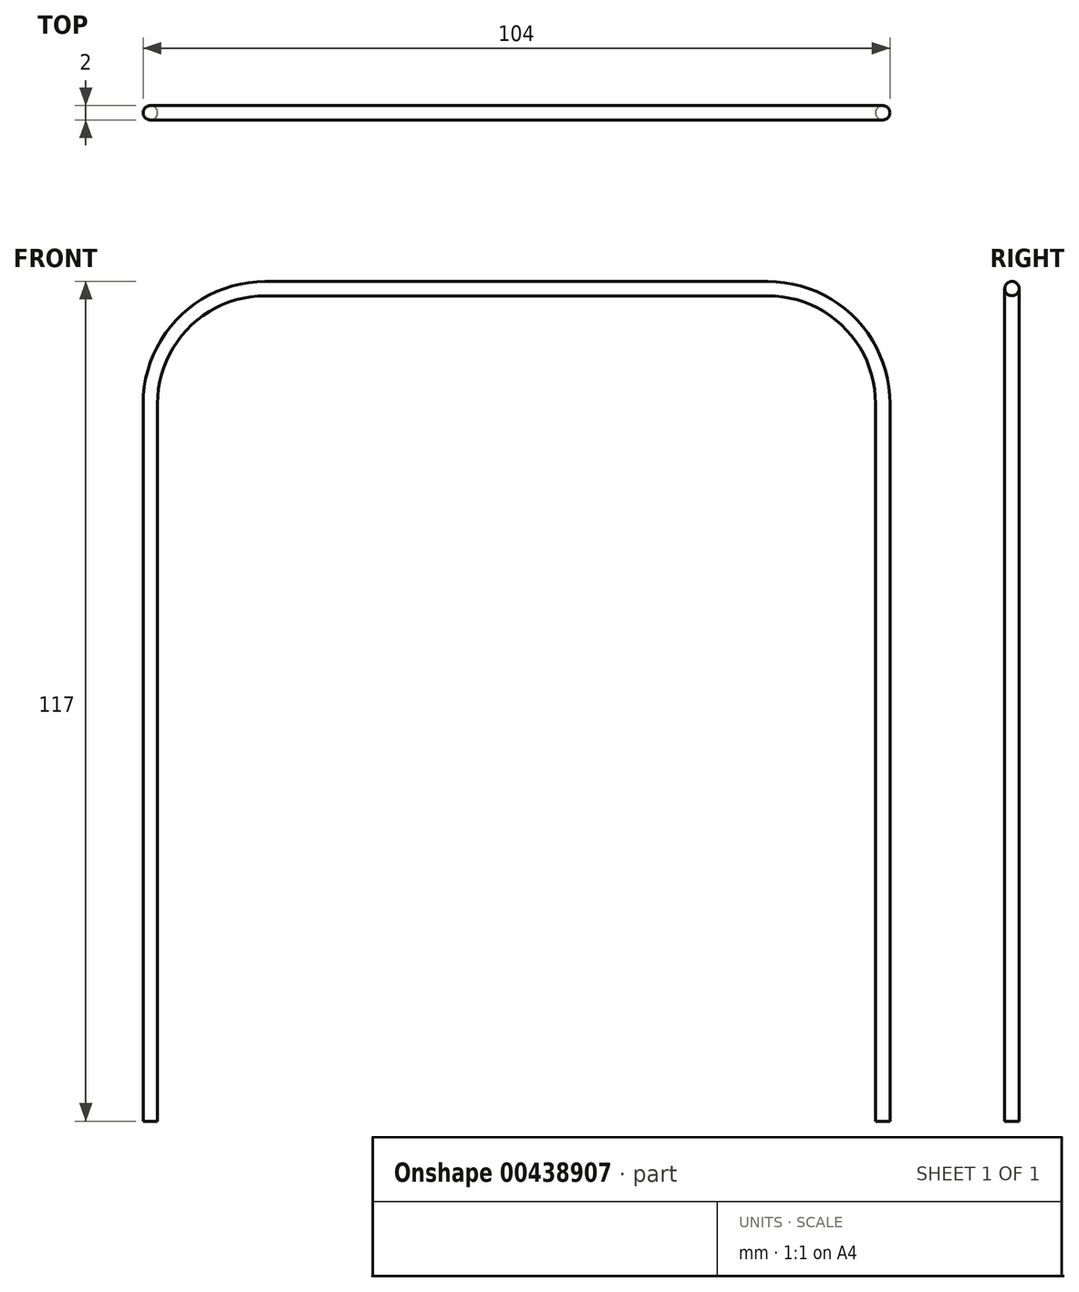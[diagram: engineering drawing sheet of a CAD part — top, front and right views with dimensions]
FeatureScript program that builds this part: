
annotation { "Feature Type Name" : "Feature", "Feature Type Description" : "" }
export const myFeature = defineFeature(function(context is Context, id is Id, definition is map)
    precondition{}
    {
        {
            var Q0;
            Q0=qCreatedBy(makeId("Front.planeOp"),FACE);
            var sketch = newSketch(context, id + "F0", { "sketchPlane" : qUnion([Q0])});
            skLineSegment(sketch, "E0", {"start": v(0, 0) * mm, "end": v(-35, 0) * mm});
            skLineSegment(sketch, "E1", {"start": v(-50, -15) * mm, "end": v(-50, -115) * mm});
            skPoint(sketch, "E2.visualSharp", {"position": v(-50, 0) * mm});
            skArc(sketch, "E2.filletArc", {"start": v(-35, 0) * mm, "mid": v(-45.6, -4.4) * mm, "end": v(-50, -15) * mm});
            skLineSegment(sketch, "E3", {"start": v(-50, -115) * mm, "end": v(-52, -115) * mm});
            skSolve(sketch);
        }
        {
            var Q0;
            Q0=qCreatedBy(makeId("Right.planeOp"),FACE);
            var sketch = newSketch(context, id + "F1", { "sketchPlane" : qUnion([Q0])});
            skCircle(sketch, "E4", {"center": v(0, 1) * mm, "radius": 1 * mm});
            skSolve(sketch);
        }
        {
            var Q0;
            Q0=makeQuery(id+"F1.imprint","IMPRINT",FACE,{"disambiguationData":[TD([[makeQuery(id+"F1.imprint","IMPRINT",EDGE,{"derivedFrom":sQuery(id+"F1.wireOp",EDGE,"E4")}),1.0]])]});
            var Q1;
            Q1=sQuery(id+"F0.wireOp",EDGE,"E0");
            var Q2;
            Q2=sQuery(id+"F0.wireOp",EDGE,"E2.filletArc");
            var Q3;
            Q3=sQuery(id+"F0.wireOp",EDGE,"E1");
            sweep(context, id + "F2", {"profiles" : qUnion([Q0]), "path" : qUnion([Q1, Q2, Q3])});
        }
        {
            var Q0;
            Q0=makeQuery(id+"F2.opSweep","SWEPT_BODY",BODY,{"disambiguationData":[OSD([sQuery(id+"F0.wireOp",EDGE,"E1"),sQuery(id+"F1.wireOp",EDGE,"E4")])]});
            var Q1;
            Q1=qCreatedBy(makeId("Right.planeOp"),FACE);
            mirror(context, id + "F3", {"operationType" : NewBodyOperationType.ADD, "entities" : qUnion([Q0]), "mirrorPlane" : qUnion([Q1])});
        }
    });
